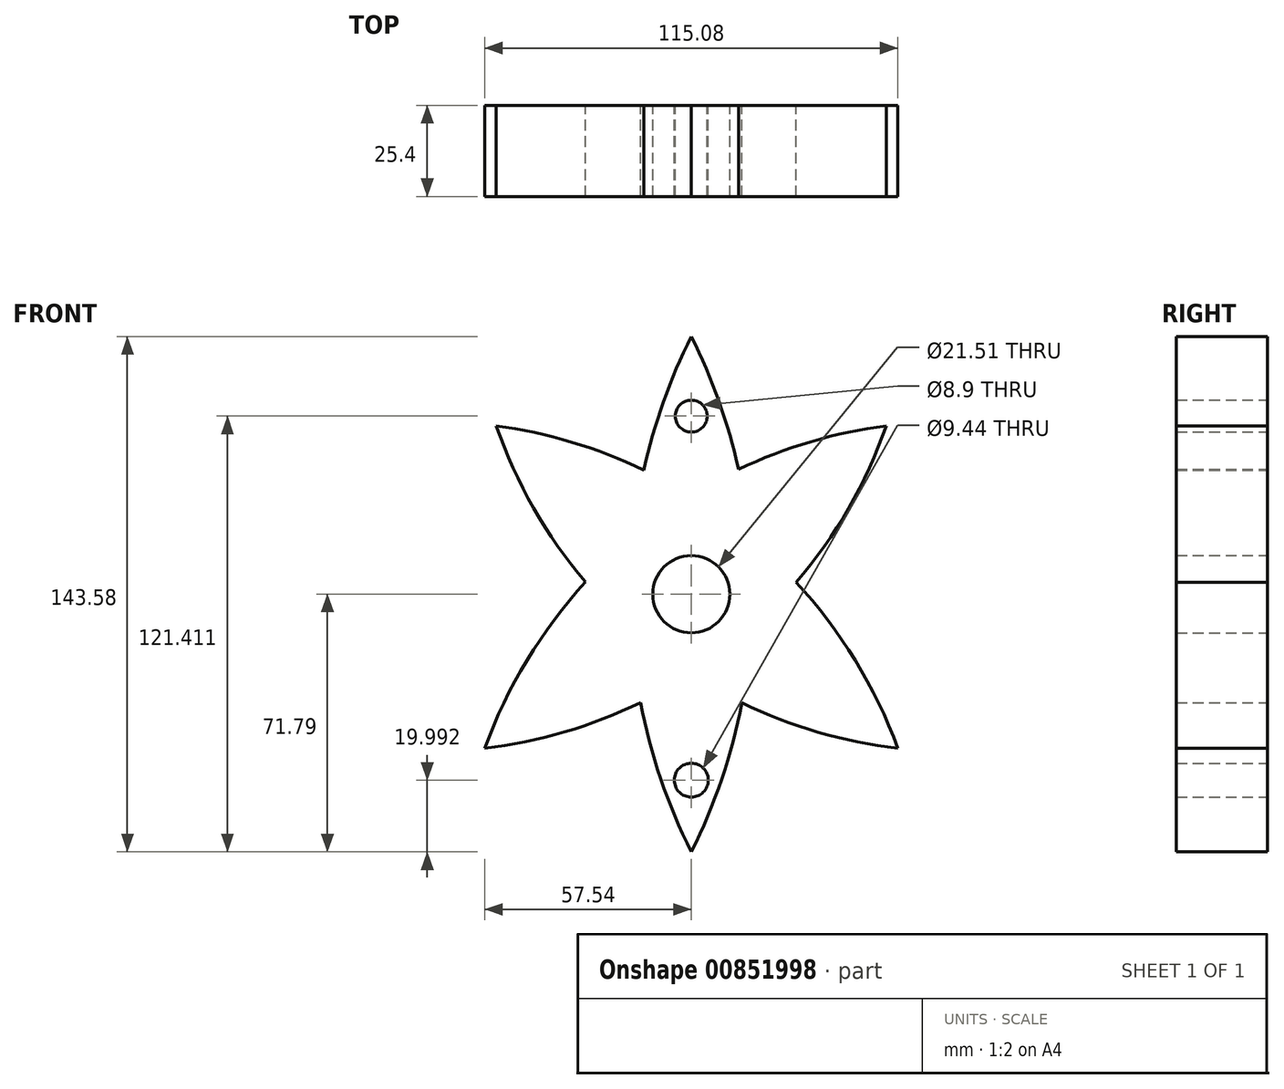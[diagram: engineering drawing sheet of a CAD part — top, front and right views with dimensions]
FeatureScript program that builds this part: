
annotation { "Feature Type Name" : "Feature", "Feature Type Description" : "" }
export const myFeature = defineFeature(function(context is Context, id is Id, definition is map)
    precondition{}
    {
        {
            var Q0;
            Q0=qCreatedBy(makeId("Front.planeOp"),FACE);
            var sketch = newSketch(context, id + "F0", { "sketchPlane" : qUnion([Q0])});
            skArc(sketch, "E0", {"start": v(0, -71.8) * mm, "mid": v(17, 0) * mm, "end": v(0, 71.8) * mm});
            skArc(sketch, "E1", {"start": v(0, 71.8) * mm, "mid": v(-17, 0) * mm, "end": v(0, -71.8) * mm});
            skArc(sketch, "E2", {"start": v(54.33, 46.92) * mm, "mid": v(-14.2, 17.67) * mm, "end": v(-57.54, -42.93) * mm});
            skArc(sketch, "E3", {"start": v(-57.54, -42.93) * mm, "mid": v(11.27, -14.04) * mm, "end": v(54.33, 46.92) * mm});
            skArc(sketch, "E4", {"start": v(-54.33, 46.92) * mm, "mid": v(-11.36, -14.14) * mm, "end": v(57.54, -42.93) * mm});
            skArc(sketch, "E5", {"start": v(57.54, -42.93) * mm, "mid": v(14.05, 17.49) * mm, "end": v(-54.33, 46.92) * mm});
            skCircle(sketch, "E6", {"center": v(0, 49.62) * mm, "radius": 4.45 * mm});
            skCircle(sketch, "E7", {"center": v(0, -51.8) * mm, "radius": 4.72 * mm});
            skCircle(sketch, "E8", {"center": v(0, 0) * mm, "radius": 10.75 * mm});
            skSolve(sketch);
        }
        {
            var Q0;
            {var subQ0=sQuery(id+"F0.wireOp",EDGE,"E5");var subQ1=sQuery(id+"F0.wireOp",EDGE,"E1");var subQ2=makeQuery(id+"F0.imprint","INTERSECT",VERTEX,{"derivedFrom":[subQ1,subQ0]});Q0=makeQuery(id+"F0.imprint","IMPRINT",FACE,{"disambiguationData":[TD([[makeQuery(id+"F0.imprint","IMPRINT",EDGE,{"disambiguationData":[TD([[subQ2,-1.0]])],"derivedFrom":subQ1}),-1.0]])]});}
            var Q1;
            Q1=makeQuery(id+"F0.imprint","IMPRINT",FACE,{"disambiguationData":[TD([[makeQuery(id+"F0.imprint","IMPRINT",EDGE,{"derivedFrom":sQuery(id+"F0.wireOp",EDGE,"E6")}),-1.0]])]});
            var Q2;
            {var subQ0=sQuery(id+"F0.wireOp",EDGE,"E2");var subQ1=sQuery(id+"F0.wireOp",EDGE,"E0");var subQ2=makeQuery(id+"F0.imprint","INTERSECT",VERTEX,{"derivedFrom":[subQ1,subQ0]});Q2=makeQuery(id+"F0.imprint","IMPRINT",FACE,{"disambiguationData":[TD([[makeQuery(id+"F0.imprint","IMPRINT",EDGE,{"disambiguationData":[TD([[subQ2,1.0]])],"derivedFrom":subQ1}),-1.0]])]});}
            var Q3;
            Q3=makeQuery(id+"F0.imprint","IMPRINT",FACE,{"disambiguationData":[TD([[makeQuery(id+"F0.imprint","IMPRINT",EDGE,{"derivedFrom":sQuery(id+"F0.wireOp",EDGE,"E8")}),-1.0]])]});
            var Q4;
            {var subQ0=sQuery(id+"F0.wireOp",EDGE,"E5");var subQ1=sQuery(id+"F0.wireOp",EDGE,"E1");var subQ2=makeQuery(id+"F0.imprint","INTERSECT",VERTEX,{"derivedFrom":[subQ1,subQ0]});Q4=makeQuery(id+"F0.imprint","IMPRINT",FACE,{"disambiguationData":[TD([[makeQuery(id+"F0.imprint","IMPRINT",EDGE,{"disambiguationData":[TD([[subQ2,-1.0]])],"derivedFrom":subQ1}),1.0]])]});}
            var Q5;
            {var subQ0=sQuery(id+"F0.wireOp",EDGE,"E2");var subQ1=sQuery(id+"F0.wireOp",EDGE,"E0");var subQ2=makeQuery(id+"F0.imprint","INTERSECT",VERTEX,{"derivedFrom":[subQ1,subQ0]});Q5=makeQuery(id+"F0.imprint","IMPRINT",FACE,{"disambiguationData":[TD([[makeQuery(id+"F0.imprint","IMPRINT",EDGE,{"disambiguationData":[TD([[subQ2,1.0]])],"derivedFrom":subQ1}),1.0]])]});}
            var Q6;
            {var subQ0=sQuery(id+"F0.wireOp",EDGE,"E3");var subQ1=sQuery(id+"F0.wireOp",EDGE,"E1");var subQ2=makeQuery(id+"F0.imprint","INTERSECT",VERTEX,{"derivedFrom":[subQ1,subQ0]});Q6=makeQuery(id+"F0.imprint","IMPRINT",FACE,{"disambiguationData":[TD([[makeQuery(id+"F0.imprint","IMPRINT",EDGE,{"disambiguationData":[TD([[subQ2,1.0]])],"derivedFrom":subQ1}),-1.0]])]});}
            var Q7;
            {var subQ0=sQuery(id+"F0.wireOp",EDGE,"E2");var subQ1=sQuery(id+"F0.wireOp",EDGE,"E1");var subQ2=makeQuery(id+"F0.imprint","INTERSECT",VERTEX,{"derivedFrom":[subQ1,subQ0]});Q7=makeQuery(id+"F0.imprint","IMPRINT",FACE,{"disambiguationData":[TD([[makeQuery(id+"F0.imprint","IMPRINT",EDGE,{"disambiguationData":[TD([[subQ2,-1.0]])],"derivedFrom":subQ1}),-1.0]])]});}
            var Q8;
            {var subQ0=sQuery(id+"F0.wireOp",EDGE,"E3");var subQ1=sQuery(id+"F0.wireOp",EDGE,"E1");var subQ2=makeQuery(id+"F0.imprint","INTERSECT",VERTEX,{"derivedFrom":[subQ1,subQ0]});Q8=makeQuery(id+"F0.imprint","IMPRINT",FACE,{"disambiguationData":[TD([[makeQuery(id+"F0.imprint","IMPRINT",EDGE,{"disambiguationData":[TD([[subQ2,1.0]])],"derivedFrom":subQ1}),1.0]])]});}
            var Q9;
            Q9=makeQuery(id+"F0.imprint","IMPRINT",FACE,{"disambiguationData":[TD([[makeQuery(id+"F0.imprint","IMPRINT",EDGE,{"derivedFrom":sQuery(id+"F0.wireOp",EDGE,"E7")}),-1.0]])]});
            var Q10;
            {var subQ0=sQuery(id+"F0.wireOp",EDGE,"E4");var subQ1=sQuery(id+"F0.wireOp",EDGE,"E0");var subQ2=makeQuery(id+"F0.imprint","INTERSECT",VERTEX,{"derivedFrom":[subQ1,subQ0]});Q10=makeQuery(id+"F0.imprint","IMPRINT",FACE,{"disambiguationData":[TD([[makeQuery(id+"F0.imprint","IMPRINT",EDGE,{"disambiguationData":[TD([[subQ2,-1.0]])],"derivedFrom":subQ1}),-1.0]])]});}
            var Q11;
            {var subQ0=sQuery(id+"F0.wireOp",EDGE,"E3");var subQ1=sQuery(id+"F0.wireOp",EDGE,"E0");var subQ2=makeQuery(id+"F0.imprint","INTERSECT",VERTEX,{"derivedFrom":[subQ1,subQ0]});Q11=makeQuery(id+"F0.imprint","IMPRINT",FACE,{"disambiguationData":[TD([[makeQuery(id+"F0.imprint","IMPRINT",EDGE,{"disambiguationData":[TD([[subQ2,-1.0]])],"derivedFrom":subQ1}),-1.0]])]});}
            var Q12;
            {var subQ0=sQuery(id+"F0.wireOp",EDGE,"E4");var subQ1=sQuery(id+"F0.wireOp",EDGE,"E0");var subQ2=makeQuery(id+"F0.imprint","INTERSECT",VERTEX,{"derivedFrom":[subQ1,subQ0]});Q12=makeQuery(id+"F0.imprint","IMPRINT",FACE,{"disambiguationData":[TD([[makeQuery(id+"F0.imprint","IMPRINT",EDGE,{"disambiguationData":[TD([[subQ2,-1.0]])],"derivedFrom":subQ1}),1.0]])]});}
            extrude(context, id + "F1", {"entities" : qUnion([Q0, Q1, Q2, Q3, Q4, Q5, Q6, Q7, Q8, Q9, Q10, Q11, Q12]), "depth" : 25.4 * mm, "offsetDistance" : 25.4 * mm});
        }
    });
